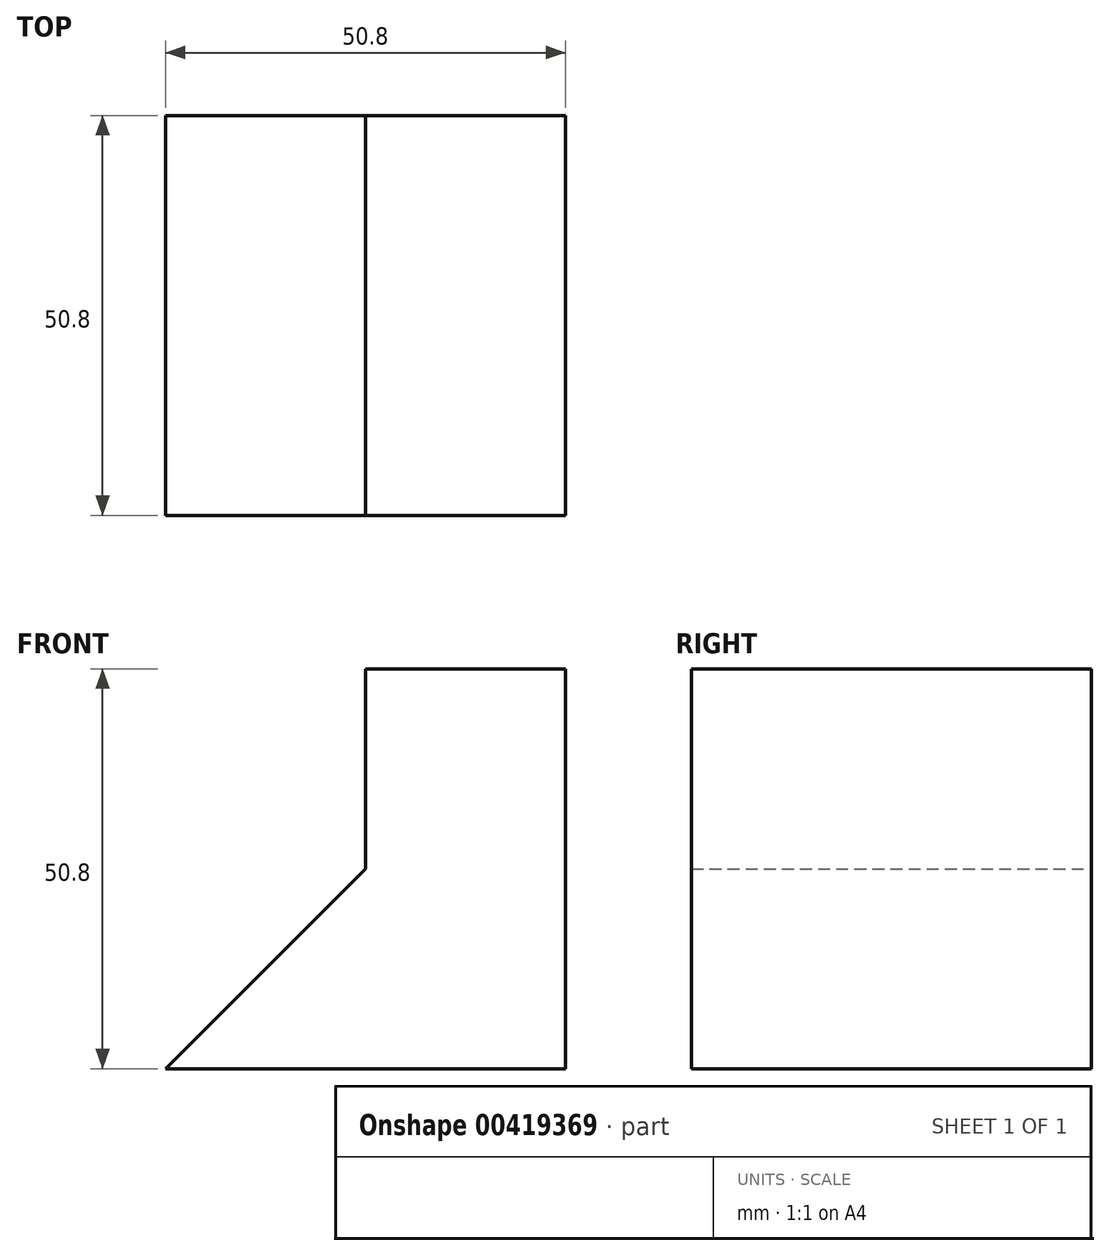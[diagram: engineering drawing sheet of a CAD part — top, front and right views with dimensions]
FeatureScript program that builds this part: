
annotation { "Feature Type Name" : "Feature", "Feature Type Description" : "" }
export const myFeature = defineFeature(function(context is Context, id is Id, definition is map)
    precondition{}
    {
        {
            var Q0;
            Q0=qCreatedBy(makeId("Front.planeOp"),FACE);
            var sketch = newSketch(context, id + "F0", { "sketchPlane" : qUnion([Q0])});
            skLineSegment(sketch, "E0", {"start": v(-35.33, 22.53) * mm, "end": v(-35.33, 47.93) * mm});
            skLineSegment(sketch, "E1", {"start": v(-35.33, 47.93) * mm, "end": v(-9.93, 47.93) * mm});
            skLineSegment(sketch, "E2", {"start": v(-9.93, 47.93) * mm, "end": v(-9.93, -2.87) * mm});
            skLineSegment(sketch, "E3", {"start": v(-9.93, -2.87) * mm, "end": v(-60.73, -2.87) * mm});
            skLineSegment(sketch, "E4", {"start": v(-60.73, -2.87) * mm, "end": v(-35.33, 22.53) * mm});
            skSolve(sketch);
        }
        {
            var Q0;
            Q0 = qSketchRegion(id + "F0", true);
            extrude(context, id + "F1", {"entities" : qUnion([Q0]), "depth" : 50.8 * mm});
        }
    });
